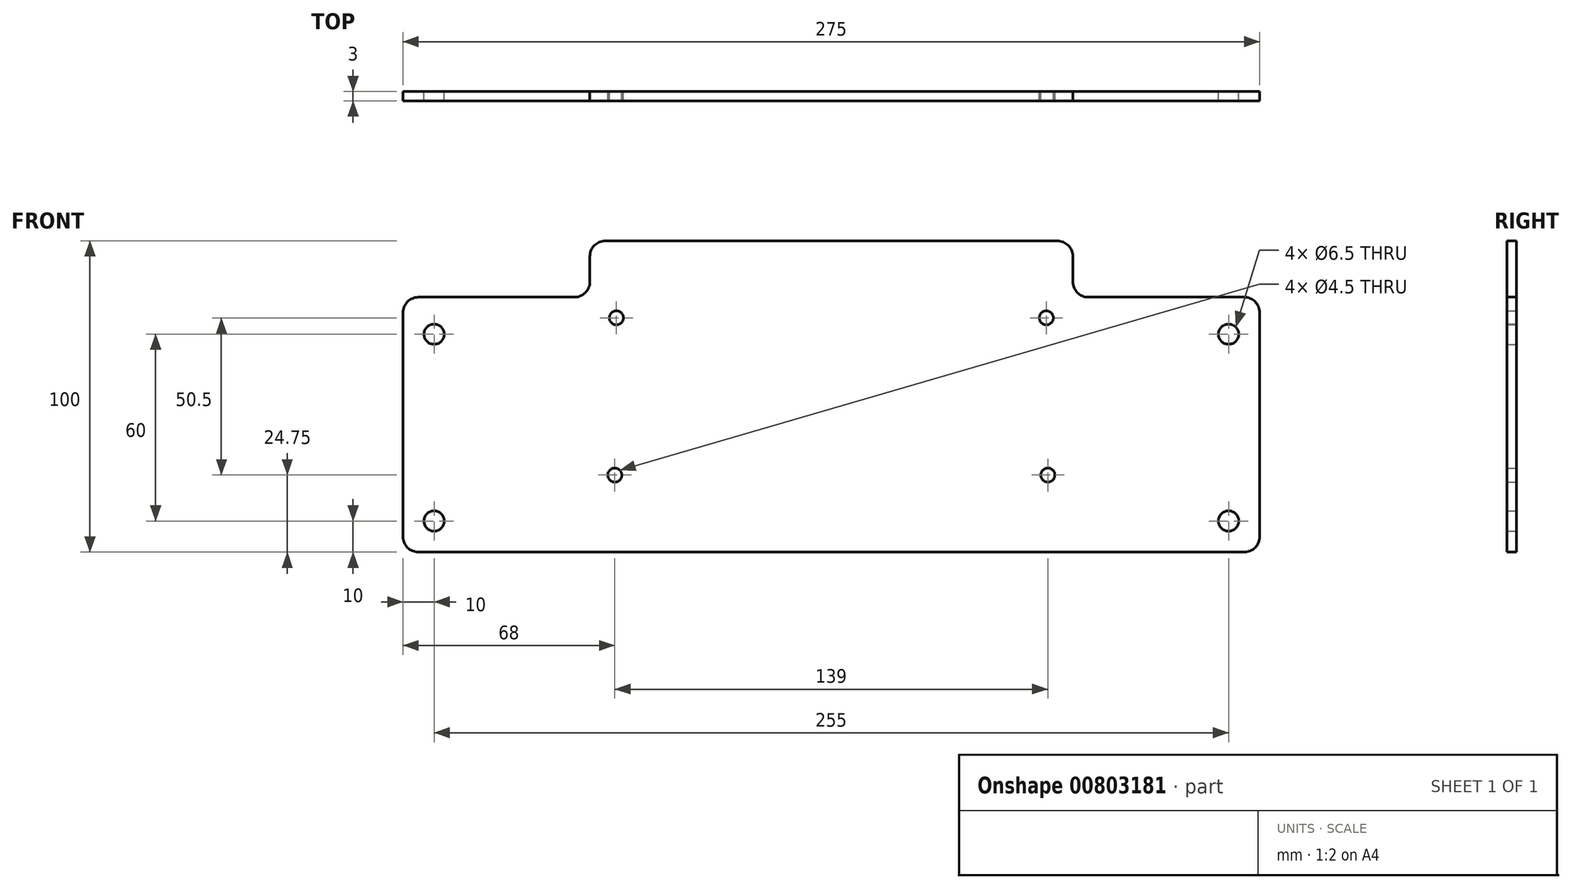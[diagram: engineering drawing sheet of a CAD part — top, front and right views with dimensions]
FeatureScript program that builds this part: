
annotation { "Feature Type Name" : "Feature", "Feature Type Description" : "" }
export const myFeature = defineFeature(function(context is Context, id is Id, definition is map)
    precondition{}
    {
        {
            var Q0;
            Q0=qCreatedBy(makeId("Front.planeOp"),FACE);
            var sketch = newSketch(context, id + "F0", { "sketchPlane" : qUnion([Q0])});
            skLineSegment(sketch, "E0.bottom", {"start": v(132.5, -50) * mm, "end": v(-132.5, -50) * mm});
            skLineSegment(sketch, "E0.top", {"start": v(72.5, 50) * mm, "end": v(-72.5, 50) * mm});
            skLineSegment(sketch, "E0.left", {"start": v(137.5, -45) * mm, "end": v(137.5, 26.89) * mm});
            skLineSegment(sketch, "E0.right", {"start": v(-137.5, -45) * mm, "end": v(-137.5, 26.89) * mm});
            skPoint(sketch, "E0.middle", {"position": v(0, 0) * mm});
            skPoint(sketch, "E1.visualSharp", {"position": v(-137.5, 50) * mm});
            skPoint(sketch, "E2.visualSharp", {"position": v(-137.5, -50) * mm});
            skArc(sketch, "E2.filletArc", {"start": v(-137.5, -45) * mm, "mid": v(-136.04, -48.54) * mm, "end": v(-132.5, -50) * mm});
            skPoint(sketch, "E3.visualSharp", {"position": v(137.5, 50) * mm});
            skPoint(sketch, "E4.visualSharp", {"position": v(137.5, -50) * mm});
            skArc(sketch, "E4.filletArc", {"start": v(132.5, -50) * mm, "mid": v(136.04, -48.54) * mm, "end": v(137.5, -45) * mm});
            skCircle(sketch, "E5", {"center": v(-69, 25.25) * mm, "radius": 2.25 * mm});
            skCircle(sketch, "E6", {"center": v(-69.5, -25.25) * mm, "radius": 2.25 * mm});
            skPoint(sketch, "E7.center.orphan", {"position": v(-69.5, 0) * mm});
            skCircle(sketch, "E8", {"center": v(69, 25.25) * mm, "radius": 2.25 * mm});
            skCircle(sketch, "E9", {"center": v(69.5, -25.25) * mm, "radius": 2.25 * mm});
            skCircle(sketch, "E10", {"center": v(-127.5, 20) * mm, "radius": 3.25 * mm});
            skCircle(sketch, "E11", {"center": v(127.5, 20) * mm, "radius": 3.25 * mm});
            skCircle(sketch, "E12", {"center": v(-127.5, -40) * mm, "radius": 3.25 * mm});
            skCircle(sketch, "E13", {"center": v(127.5, -40) * mm, "radius": 3.25 * mm});
            skLineSegment(sketch, "E14", {"start": v(-132.5, 31.89) * mm, "end": v(-82.5, 31.89) * mm});
            skLineSegment(sketch, "E15", {"start": v(-77.5, 36.89) * mm, "end": v(-77.5, 45) * mm});
            skLineSegment(sketch, "E16", {"start": v(82.5, 31.89) * mm, "end": v(132.5, 31.89) * mm});
            skLineSegment(sketch, "E17", {"start": v(77.5, 36.89) * mm, "end": v(77.5, 45) * mm});
            skPoint(sketch, "E18.orphan", {"position": v(69, 31.89) * mm});
            skPoint(sketch, "E19.visualSharp", {"position": v(-137.5, 31.89) * mm});
            skArc(sketch, "E19.filletArc", {"start": v(-132.5, 31.89) * mm, "mid": v(-136.04, 30.42) * mm, "end": v(-137.5, 26.89) * mm});
            skPoint(sketch, "E20.visualSharp", {"position": v(-77.5, 31.89) * mm});
            skArc(sketch, "E20.filletArc", {"start": v(-82.5, 31.89) * mm, "mid": v(-78.96, 33.35) * mm, "end": v(-77.5, 36.89) * mm});
            skPoint(sketch, "E21.visualSharp", {"position": v(-77.5, 50) * mm});
            skArc(sketch, "E21.filletArc", {"start": v(-72.5, 50) * mm, "mid": v(-76.04, 48.54) * mm, "end": v(-77.5, 45) * mm});
            skPoint(sketch, "E22.visualSharp", {"position": v(77.5, 50) * mm});
            skArc(sketch, "E22.filletArc", {"start": v(77.5, 45) * mm, "mid": v(76.04, 48.54) * mm, "end": v(72.5, 50) * mm});
            skPoint(sketch, "E23.visualSharp", {"position": v(77.5, 31.89) * mm});
            skArc(sketch, "E23.filletArc", {"start": v(77.5, 36.89) * mm, "mid": v(78.96, 33.35) * mm, "end": v(82.5, 31.89) * mm});
            skPoint(sketch, "E24.visualSharp", {"position": v(137.5, 31.89) * mm});
            skArc(sketch, "E24.filletArc", {"start": v(137.5, 26.89) * mm, "mid": v(136.04, 30.42) * mm, "end": v(132.5, 31.89) * mm});
            skLineSegment(sketch, "E25", {"start": v(-69, 25.25) * mm, "end": v(-69, 34.4) * mm});
            skLineSegment(sketch, "E26", {"start": v(-69, 34.4) * mm, "end": v(-69, 15.19) * mm});
            skSolve(sketch);
        }
        {
            var Q0;
            Q0=makeQuery(id+"F0.imprint","IMPRINT",FACE,{"disambiguationData":[TD([[makeQuery(id+"F0.imprint","IMPRINT",EDGE,{"derivedFrom":sQuery(id+"F0.wireOp",EDGE,"E0.bottom")}),-1.0]])]});
            extrude(context, id + "F1", {"entities" : qUnion([Q0]), "depth" : 3 * mm, "offsetDistance" : 25 * mm});
        }
    });
